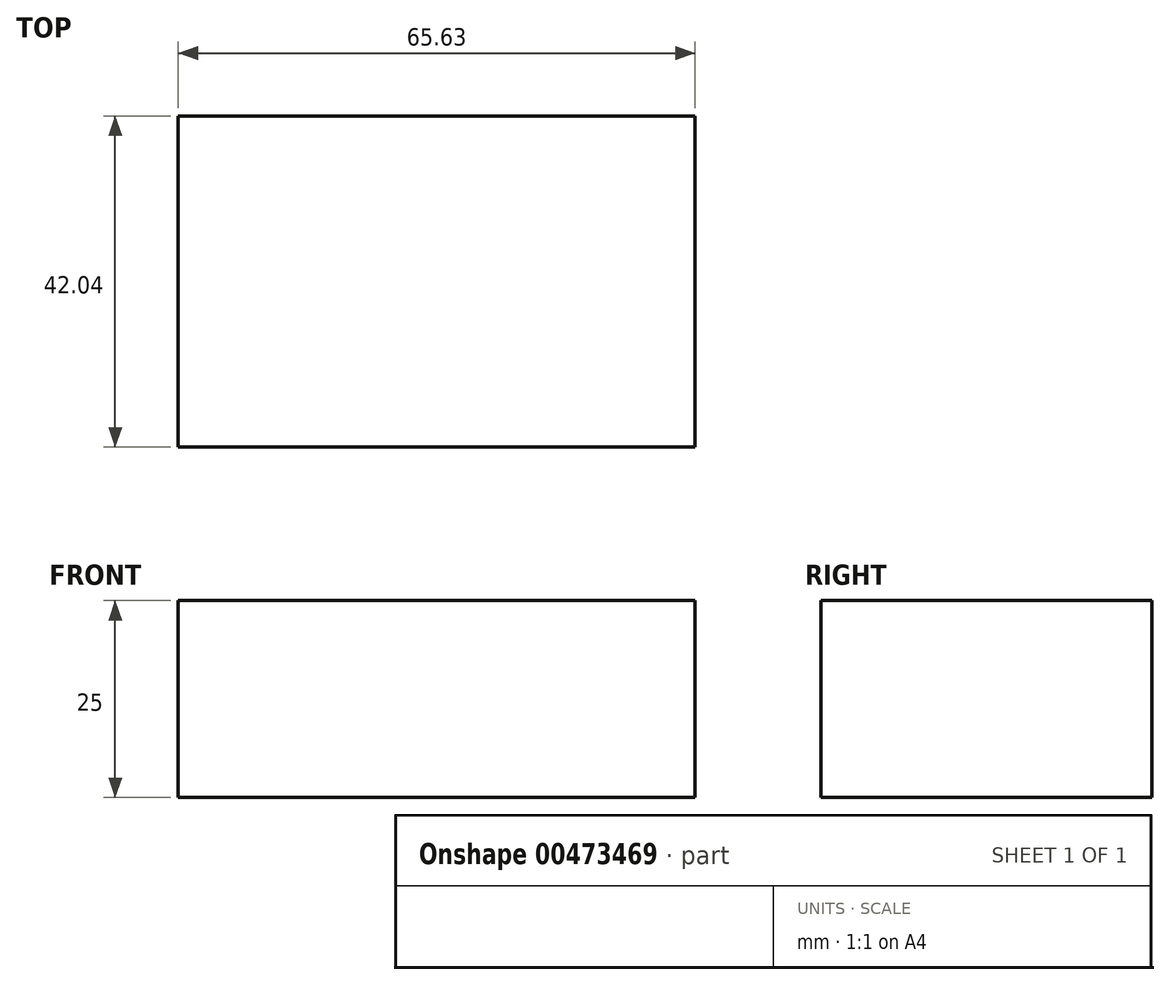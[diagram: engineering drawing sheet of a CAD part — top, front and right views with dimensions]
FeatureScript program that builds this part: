
annotation { "Feature Type Name" : "Feature", "Feature Type Description" : "" }
export const myFeature = defineFeature(function(context is Context, id is Id, definition is map)
    precondition{}
    {
        {
            var Q0;
            Q0=qCreatedBy(makeId("Top.planeOp"),FACE);
            var sketch = newSketch(context, id + "F0", { "sketchPlane" : qUnion([Q0])});
            skLineSegment(sketch, "E0.bottom", {"start": v(-30.44, -8.32) * mm, "end": v(35.19, -8.32) * mm});
            skLineSegment(sketch, "E0.top", {"start": v(-30.44, 33.72) * mm, "end": v(35.19, 33.72) * mm});
            skLineSegment(sketch, "E0.left", {"start": v(-30.44, -8.32) * mm, "end": v(-30.44, 33.72) * mm});
            skLineSegment(sketch, "E0.right", {"start": v(35.19, -8.32) * mm, "end": v(35.19, 33.72) * mm});
            skSolve(sketch);
        }
        {
            var Q0;
            Q0=makeQuery(id+"F0.imprint","IMPRINT",FACE,{"disambiguationData":[TD([[makeQuery(id+"F0.imprint","IMPRINT",EDGE,{"derivedFrom":sQuery(id+"F0.wireOp",EDGE,"E0.bottom")}),1.0]])]});
            extrude(context, id + "F1", {"entities" : qUnion([Q0]), "depth" : 25 * mm});
        }
    });
